# Revit family: Legrand_Lighting_Management_KNX_Actuator
name_source: partatom
category: Dispositifs d'éclairage
units: mm (PartAtom-declared; Revit-internal decimal feet)

## family parameters
Conserver l'orientation des annotations = Non
Cote de connecteur circulaire = Utiliser le diamètre
Couper avec des vides une fois chargée = Non
Hôte = Face
Partagée = Non
Point de calcul de pièce = Non
Type d'élément = Normal

## types (2) — shared parameters
Alarm function = Non
Collecteur de terre = Non
Colour = <Par catégorie>
Constant light control = Non
Cosses d'artère secondaire = Non
Degree of protection (IP) = IP20
Dim function with dimmer basic element = Non
Elévation par défaut = 1219 mm
Fabricant = Legrand
Forced switch off = Non
General Conditions of Use = https://export.legrand.com
HVAC-control = Non
Liaison neutre = Non
Mounting method = Other
Remote operation = Non
Response value luminosity adjustable = Non
Response value sensitivity adjustable = Non
Substation input = Non
Suitable for wireless transmission = Non
URL = http://www.legrandoc.com
zero-valued in all types: Detection angle horizontal (MAX) (°), Detection angle horizontal (MIN) (°), Diameter detection range on floor (m), Frequency (MAX) (Hz), Frequency (MIN) (Hz), Max. duty cycle (mn), Max. starting current (A), Max. switching power (W), Max. transmission range frontally (m), Max. transmission range sideways (m), Maximum mounting height (m), Min. switch-on time (s), Nominal voltage (V), RAL-number (akin), Response value luminosity (MAX) (lx), Response value luminosity (MIN) (lx), Temperature (MAX) (°C), Temperature (MIN) (°C)

## per-type parameters (varying)
| type | DALI 4 sorties | Description | Modèle | Variation 10-10V 4 sorties |
| Dimming 1-10V 4 outputs | Non | KNX FALSE CEILING CONTROLLER 4 OUTPUTS 1-10V | 048887 | Oui |
| DALI 4 outputs | Oui | KNX FALSE CEILING CONTROLLER 4 OUTPUTS DALI | 048888 | Non |
